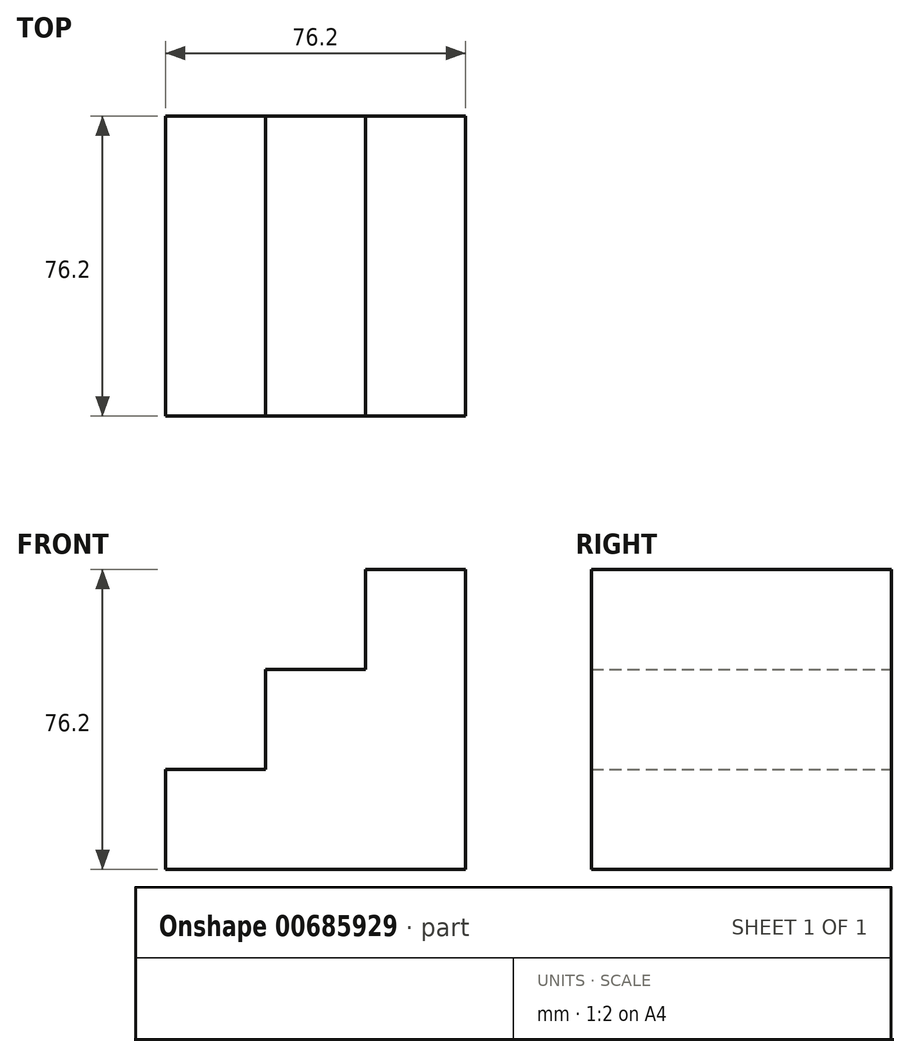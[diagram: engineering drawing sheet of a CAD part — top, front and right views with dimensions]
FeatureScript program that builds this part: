
annotation { "Feature Type Name" : "Feature", "Feature Type Description" : "" }
export const myFeature = defineFeature(function(context is Context, id is Id, definition is map)
    precondition{}
    {
        {
            var Q0;
            Q0=qCreatedBy(makeId("Front.planeOp"),FACE);
            var sketch = newSketch(context, id + "F0", { "sketchPlane" : qUnion([Q0])});
            skLineSegment(sketch, "E0", {"start": v(0, 0) * mm, "end": v(0, 76.2) * mm});
            skLineSegment(sketch, "E1", {"start": v(0, 76.2) * mm, "end": v(-25.4, 76.2) * mm});
            skLineSegment(sketch, "E2", {"start": v(-25.4, 76.2) * mm, "end": v(-25.4, 50.8) * mm});
            skLineSegment(sketch, "E3", {"start": v(-25.4, 50.8) * mm, "end": v(-50.8, 50.8) * mm});
            skLineSegment(sketch, "E4", {"start": v(-50.8, 50.8) * mm, "end": v(-50.8, 25.4) * mm});
            skLineSegment(sketch, "E5", {"start": v(-50.8, 25.4) * mm, "end": v(-76.2, 25.4) * mm});
            skLineSegment(sketch, "E6", {"start": v(-76.2, 25.4) * mm, "end": v(-76.2, 0) * mm});
            skLineSegment(sketch, "E7", {"start": v(-76.2, 0) * mm, "end": v(0, 0) * mm});
            skSolve(sketch);
        }
        {
            var Q0;
            Q0 = qSketchRegion(id + "F0", true);
            extrude(context, id + "F1", {"entities" : qUnion([Q0]), "depth" : 76.2 * mm, "offsetDistance" : 25.4 * mm});
        }
    });
